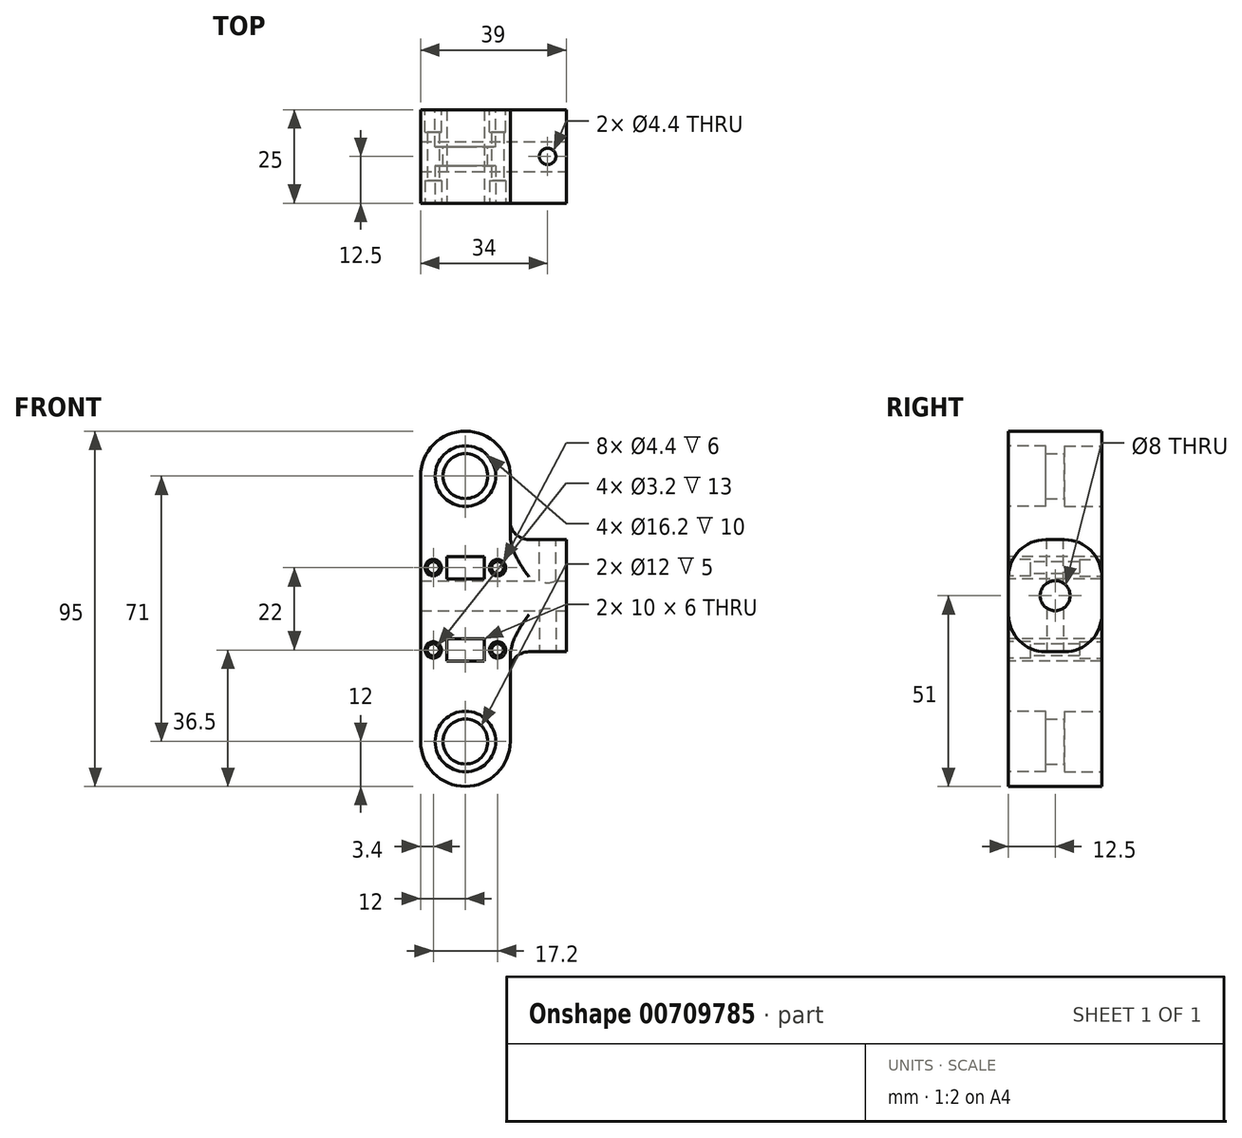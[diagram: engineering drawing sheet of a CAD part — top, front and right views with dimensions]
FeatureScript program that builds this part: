
annotation { "Feature Type Name" : "Feature", "Feature Type Description" : "" }
export const myFeature = defineFeature(function(context is Context, id is Id, definition is map)
    precondition{}
    {
        {
            var Q0;
            Q0=qCreatedBy(makeId("Front.planeOp"),FACE);
            var sketch = newSketch(context, id + "F0", { "sketchPlane" : qUnion([Q0])});
            skCircle(sketch, "E0", {"center": v(0, 35.5) * mm, "radius": 6 * mm});
            skCircle(sketch, "E1", {"center": v(0, -35.5) * mm, "radius": 6 * mm});
            skCircle(sketch, "E2", {"center": v(0, 35.5) * mm, "radius": 12.5 * mm, "construction": true});
            skCircle(sketch, "E3", {"center": v(0, -35.5) * mm, "radius": 12.5 * mm, "construction": true});
            skCircle(sketch, "E4", {"center": v(0, 35.5) * mm, "radius": 8 * mm, "construction": true});
            skCircle(sketch, "E5", {"center": v(0, 35.5) * mm, "radius": 12 * mm});
            skCircle(sketch, "E6", {"center": v(0, -35.5) * mm, "radius": 12 * mm});
            skLineSegment(sketch, "E7", {"start": v(-12, 35.5) * mm, "end": v(-12, -35.5) * mm});
            skLineSegment(sketch, "E8", {"start": v(12, 35.5) * mm, "end": v(12, -35.5) * mm});
            skLineSegment(sketch, "E9", {"start": v(12, 18.5) * mm, "end": v(27, 18.5) * mm});
            skLineSegment(sketch, "E10", {"start": v(27, 18.5) * mm, "end": v(27, -11.5) * mm});
            skLineSegment(sketch, "E11", {"start": v(27, -11.5) * mm, "end": v(12, -11.5) * mm});
            skSolve(sketch);
        }
        {
            var Q0;
            {var subQ4=sQuery(id+"F0.wireOp",EDGE,"E7");Q0=makeQuery(id+"F0.imprint","IMPRINT",FACE,{"disambiguationData":[TD([[makeQuery(id+"F0.imprint","IMPRINT",EDGE,{"derivedFrom":subQ4}),1.0]])]});}
            var Q1;
            Q1=makeQuery(id+"F0.imprint","IMPRINT",FACE,{"disambiguationData":[TD([[makeQuery(id+"F0.imprint","IMPRINT",EDGE,{"derivedFrom":sQuery(id+"F0.wireOp",EDGE,"E0")}),-1.0]])]});
            var Q2;
            Q2=makeQuery(id+"F0.imprint","IMPRINT",FACE,{"disambiguationData":[TD([[makeQuery(id+"F0.imprint","IMPRINT",EDGE,{"derivedFrom":sQuery(id+"F0.wireOp",EDGE,"E1")}),-1.0]])]});
            var Q3;
            {var subQ0=sQuery(id+"F0.wireOp",EDGE,"E9");Q3=makeQuery(id+"F0.imprint","IMPRINT",FACE,{"disambiguationData":[TD([[makeQuery(id+"F0.imprint","IMPRINT",EDGE,{"derivedFrom":subQ0}),-1.0]])]});}
            extrude(context, id + "F1", {"entities" : qUnion([Q0, Q1, Q2, Q3]), "depth" : 25 * mm, "offsetDistance" : 25 * mm});
        }
        {
            var Q0;
            Q0=makeQuery(id+"F1.opExtrude","CAP_FACE",FACE,{"disambiguationData":[OSD([sQuery(id+"F0.wireOp",EDGE,"E0"),sQuery(id+"F0.wireOp",EDGE,"E1"),sQuery(id+"F0.wireOp",EDGE,"E5"),sQuery(id+"F0.wireOp",EDGE,"E6"),sQuery(id+"F0.wireOp",EDGE,"E7"),sQuery(id+"F0.wireOp",EDGE,"E8"),sQuery(id+"F0.wireOp",EDGE,"E9"),sQuery(id+"F0.wireOp",EDGE,"E10"),sQuery(id+"F0.wireOp",EDGE,"E11")])],"isStart":false});
            var sketch = newSketch(context, id + "F2", { "sketchPlane" : qUnion([Q0])});
            skCircle(sketch, "E12", {"center": v(0, 35.5) * mm, "radius": 8.1 * mm});
            skCircle(sketch, "E13", {"center": v(0, -35.5) * mm, "radius": 8.1 * mm});
            skSolve(sketch);
        }
        {
            var Q0;
            Q0=makeQuery(id+"F2.imprint","IMPRINT",FACE,{"disambiguationData":[TD([[makeQuery(id+"F2.imprint","IMPRINT",EDGE,{"derivedFrom":sQuery(id+"F2.wireOp",EDGE,"E12")}),1.0]])]});
            var Q1;
            Q1=makeQuery(id+"F2.imprint","IMPRINT",FACE,{"disambiguationData":[TD([[makeQuery(id+"F2.imprint","IMPRINT",EDGE,{"derivedFrom":sQuery(id+"F2.wireOp",EDGE,"E13")}),1.0]])]});
            extrude(context, id + "F3", {"entities" : qUnion([Q0, Q1]), "operationType" : NewBodyOperationType.REMOVE, "oppositeDirection" : true, "depth" : 10 * mm, "offsetDistance" : 25 * mm});
        }
        {
            var Q0;
            Q0=makeQuery(id+"F1.opExtrude","CAP_FACE",FACE,{"disambiguationData":[OSD([sQuery(id+"F0.wireOp",EDGE,"E0"),sQuery(id+"F0.wireOp",EDGE,"E1"),sQuery(id+"F0.wireOp",EDGE,"E5"),sQuery(id+"F0.wireOp",EDGE,"E6"),sQuery(id+"F0.wireOp",EDGE,"E7"),sQuery(id+"F0.wireOp",EDGE,"E8"),sQuery(id+"F0.wireOp",EDGE,"E9"),sQuery(id+"F0.wireOp",EDGE,"E10"),sQuery(id+"F0.wireOp",EDGE,"E11")])],"isStart":true});
            var sketch = newSketch(context, id + "F4", { "sketchPlane" : qUnion([Q0])});
            skCircle(sketch, "E14.0", {"center": v(0, 35.5) * mm, "radius": 8.1 * mm});
            skCircle(sketch, "E15.0", {"center": v(0, -35.5) * mm, "radius": 8.1 * mm});
            skSolve(sketch);
        }
        {
            var Q0;
            Q0=makeQuery(id+"F4.imprint","IMPRINT",FACE,{"disambiguationData":[TD([[makeQuery(id+"F4.imprint","IMPRINT",EDGE,{"derivedFrom":sQuery(id+"F4.wireOp",EDGE,"E14.0")}),1.0]])]});
            var Q1;
            Q1=makeQuery(id+"F4.imprint","IMPRINT",FACE,{"disambiguationData":[TD([[makeQuery(id+"F4.imprint","IMPRINT",EDGE,{"derivedFrom":sQuery(id+"F4.wireOp",EDGE,"E15.0")}),1.0]])]});
            extrude(context, id + "F5", {"entities" : qUnion([Q0, Q1]), "operationType" : NewBodyOperationType.REMOVE, "oppositeDirection" : true, "depth" : 10 * mm, "offsetDistance" : 25 * mm});
        }
        {
            var Q0;
            Q0=makeQuery(id+"F1.opExtrude","SWEPT_FACE",FACE,{"disambiguationData":[OSD([sQuery(id+"F0.wireOp",EDGE,"E10")])]});
            var sketch = newSketch(context, id + "F6", { "sketchPlane" : qUnion([Q0])});
            skCircle(sketch, "E16", {"center": v(-12.5, 3.5) * mm, "radius": 4 * mm});
            skPoint(sketch, "E16.centerSnap0", {"position": v(-12.5, 18.5) * mm});
            skSolve(sketch);
        }
        {
            var Q0;
            Q0=makeQuery(id+"F6.imprint","IMPRINT",FACE,{"disambiguationData":[TD([[makeQuery(id+"F6.imprint","IMPRINT",EDGE,{"derivedFrom":sQuery(id+"F6.wireOp",EDGE,"E16")}),1.0]])]});
            extrude(context, id + "F7", {"entities" : qUnion([Q0]), "operationType" : NewBodyOperationType.REMOVE, "endBound" : BoundingType.THROUGH_ALL, "oppositeDirection" : true, "depth" : 25 * mm, "offsetDistance" : 25 * mm});
        }
        {
            var Q0;
            Q0=makeQuery(id+"F1.opExtrude","CAP_EDGE",EDGE,{"disambiguationData":[OSD([sQuery(id+"F0.wireOp",EDGE,"E9")])],"isStart":false});
            var Q1;
            Q1=makeQuery(id+"F1.opExtrude","CAP_EDGE",EDGE,{"disambiguationData":[OSD([sQuery(id+"F0.wireOp",EDGE,"E9")])],"isStart":true});
            var Q2;
            Q2=makeQuery(id+"F1.opExtrude","CAP_EDGE",EDGE,{"disambiguationData":[OSD([sQuery(id+"F0.wireOp",EDGE,"E11")])],"isStart":false});
            var Q3;
            Q3=makeQuery(id+"F1.opExtrude","CAP_EDGE",EDGE,{"disambiguationData":[OSD([sQuery(id+"F0.wireOp",EDGE,"E11")])],"isStart":true});
            fillet(context, id + "F8", {"entities" : qUnion([Q0, Q1, Q2, Q3]), "radius" : 10 * mm, "allowEdgeOverflow" : false});
        }
        {
            var Q0;
            Q0=makeQuery(id+"F1.opExtrude","SWEPT_EDGE",EDGE,{"disambiguationData":[OSD([sQuery(id+"F0.wireOp",EDGE,"E8"),sQuery(id+"F0.wireOp",EDGE,"E9")])]});
            var Q1;
            Q1=makeQuery(id+"F1.opExtrude","SWEPT_EDGE",EDGE,{"disambiguationData":[OSD([sQuery(id+"F0.wireOp",EDGE,"E8"),sQuery(id+"F0.wireOp",EDGE,"E11")])]});
            fillet(context, id + "F9", {"entities" : qUnion([Q0, Q1]), "radius" : 5 * mm, "tangentPropagation" : true, "allowEdgeOverflow" : false});
        }
        {
            var Q0;
            Q0=makeQuery(id+"F1.opExtrude","SWEPT_FACE",FACE,{"disambiguationData":[OSD([sQuery(id+"F0.wireOp",EDGE,"E9")])]});
            var sketch = newSketch(context, id + "F10", { "sketchPlane" : qUnion([Q0])});
            skCircle(sketch, "E17", {"center": v(22, -12.5) * mm, "radius": 2.2 * mm});
            skPoint(sketch, "E17.centerSnap0", {"position": v(17, -12.5) * mm});
            skPoint(sketch, "E17.centerSnap1", {"position": v(22, -10) * mm});
            skSolve(sketch);
        }
        {
            var Q0;
            Q0=makeQuery(id+"F10.imprint","IMPRINT",FACE,{"disambiguationData":[TD([[makeQuery(id+"F10.imprint","IMPRINT",EDGE,{"derivedFrom":sQuery(id+"F10.wireOp",EDGE,"E17")}),1.0]])]});
            extrude(context, id + "F11", {"entities" : qUnion([Q0]), "operationType" : NewBodyOperationType.REMOVE, "endBound" : BoundingType.UP_TO_NEXT, "oppositeDirection" : true, "depth" : 25 * mm, "offsetDistance" : 25 * mm});
        }
        {
            var Q0;
            Q0=makeQuery(id+"F1.opExtrude","SWEPT_FACE",FACE,{"disambiguationData":[OSD([sQuery(id+"F0.wireOp",EDGE,"E11")])]});
            var sketch = newSketch(context, id + "F12", { "sketchPlane" : qUnion([Q0])});
            skCircle(sketch, "E18.0", {"center": v(22, 12.5) * mm, "radius": 2.2 * mm});
            skSolve(sketch);
        }
        {
            var Q0;
            Q0=makeQuery(id+"F12.imprint","IMPRINT",FACE,{"disambiguationData":[TD([[makeQuery(id+"F12.imprint","IMPRINT",EDGE,{"derivedFrom":sQuery(id+"F12.wireOp",EDGE,"E18.0")}),1.0]])]});
            extrude(context, id + "F13", {"entities" : qUnion([Q0]), "operationType" : NewBodyOperationType.REMOVE, "endBound" : BoundingType.UP_TO_NEXT, "oppositeDirection" : true, "depth" : 25 * mm, "offsetDistance" : 25 * mm});
        }
        {
            var Q0;
            Q0=makeQuery(id+"F1.opExtrude","CAP_FACE",FACE,{"disambiguationData":[OSD([sQuery(id+"F0.wireOp",EDGE,"E0"),sQuery(id+"F0.wireOp",EDGE,"E1"),sQuery(id+"F0.wireOp",EDGE,"E5"),sQuery(id+"F0.wireOp",EDGE,"E6"),sQuery(id+"F0.wireOp",EDGE,"E7"),sQuery(id+"F0.wireOp",EDGE,"E8"),sQuery(id+"F0.wireOp",EDGE,"E9"),sQuery(id+"F0.wireOp",EDGE,"E10"),sQuery(id+"F0.wireOp",EDGE,"E11")])],"isStart":false});
            var sketch = newSketch(context, id + "F14", { "sketchPlane" : qUnion([Q0])});
            skLineSegment(sketch, "E19.bottom", {"start": v(-3, 12) * mm, "end": v(3, 12) * mm, "construction": true});
            skLineSegment(sketch, "E19.top", {"start": v(-3, 10) * mm, "end": v(3, 10) * mm, "construction": true});
            skLineSegment(sketch, "E19.left", {"start": v(-3, 12) * mm, "end": v(-3, 10) * mm, "construction": true});
            skLineSegment(sketch, "E19.right", {"start": v(3, 12) * mm, "end": v(3, 10) * mm, "construction": true});
            skLineSegment(sketch, "E20.bottom", {"start": v(-3, -10) * mm, "end": v(3, -10) * mm, "construction": true});
            skLineSegment(sketch, "E20.top", {"start": v(-3, -12) * mm, "end": v(3, -12) * mm, "construction": true});
            skLineSegment(sketch, "E20.left", {"start": v(-3, -10) * mm, "end": v(-3, -12) * mm, "construction": true});
            skLineSegment(sketch, "E20.right", {"start": v(3, -10) * mm, "end": v(3, -12) * mm, "construction": true});
            skLineSegment(sketch, "E21", {"start": v(0, 0) * mm, "end": v(0, -10) * mm, "construction": true});
            skLineSegment(sketch, "E22.bottom", {"start": v(5, 8) * mm, "end": v(-5, 8) * mm});
            skLineSegment(sketch, "E22.top", {"start": v(5, 14) * mm, "end": v(-5, 14) * mm});
            skLineSegment(sketch, "E22.left", {"start": v(5, 8) * mm, "end": v(5, 14) * mm});
            skLineSegment(sketch, "E22.right", {"start": v(-5, 8) * mm, "end": v(-5, 14) * mm});
            skPoint(sketch, "E22.middle", {"position": v(0, 11) * mm});
            skPoint(sketch, "E22.middle.positionSnap0", {"position": v(0, 12) * mm});
            skPoint(sketch, "E22.middle.positionSnap1", {"position": v(3, 11) * mm});
            skPoint(sketch, "E22.centerSnap0", {"position": v(0, 12) * mm});
            skPoint(sketch, "E22.centerSnap1", {"position": v(3, 11) * mm});
            skLineSegment(sketch, "E23.bottom", {"start": v(5, -14) * mm, "end": v(-5, -14) * mm});
            skLineSegment(sketch, "E23.top", {"start": v(5, -8) * mm, "end": v(-5, -8) * mm});
            skLineSegment(sketch, "E23.left", {"start": v(5, -14) * mm, "end": v(5, -8) * mm});
            skLineSegment(sketch, "E23.right", {"start": v(-5, -14) * mm, "end": v(-5, -8) * mm});
            skPoint(sketch, "E23.middle", {"position": v(0, -11) * mm});
            skPoint(sketch, "E23.middle.positionSnap0", {"position": v(3, -11) * mm});
            skPoint(sketch, "E23.middle.positionSnap1", {"position": v(0, -12) * mm});
            skPoint(sketch, "E23.centerSnap0", {"position": v(3, -11) * mm});
            skPoint(sketch, "E23.centerSnap1", {"position": v(0, -12) * mm});
            skCircle(sketch, "E24", {"center": v(-8.6, 11) * mm, "radius": 1.6 * mm});
            skPoint(sketch, "E24.centerSnap0", {"position": v(-5, 11) * mm});
            skCircle(sketch, "E25", {"center": v(8.6, 11) * mm, "radius": 1.6 * mm});
            skPoint(sketch, "E25.centerSnap0", {"position": v(5, 11) * mm});
            skCircle(sketch, "E26", {"center": v(-8.6, -11) * mm, "radius": 1.6 * mm});
            skPoint(sketch, "E26.centerSnap0", {"position": v(-5, -11) * mm});
            skCircle(sketch, "E27", {"center": v(8.6, -11) * mm, "radius": 1.6 * mm});
            skPoint(sketch, "E27.centerSnap0", {"position": v(5, -11) * mm});
            skSolve(sketch);
        }
        {
            var Q0;
            Q0=makeQuery(id+"F14.imprint","IMPRINT",FACE,{"disambiguationData":[TD([[makeQuery(id+"F14.imprint","IMPRINT",EDGE,{"derivedFrom":sQuery(id+"F14.wireOp",EDGE,"E24")}),1.0]])]});
            var Q1;
            Q1=makeQuery(id+"F14.imprint","IMPRINT",FACE,{"disambiguationData":[TD([[makeQuery(id+"F14.imprint","IMPRINT",EDGE,{"derivedFrom":sQuery(id+"F14.wireOp",EDGE,"E22.bottom")}),-1.0]])]});
            var Q2;
            Q2=makeQuery(id+"F14.imprint","IMPRINT",FACE,{"disambiguationData":[TD([[makeQuery(id+"F14.imprint","IMPRINT",EDGE,{"derivedFrom":sQuery(id+"F14.wireOp",EDGE,"E25")}),1.0]])]});
            var Q3;
            Q3=makeQuery(id+"F14.imprint","IMPRINT",FACE,{"disambiguationData":[TD([[makeQuery(id+"F14.imprint","IMPRINT",EDGE,{"derivedFrom":sQuery(id+"F14.wireOp",EDGE,"E27")}),1.0]])]});
            var Q4;
            Q4=makeQuery(id+"F14.imprint","IMPRINT",FACE,{"disambiguationData":[TD([[makeQuery(id+"F14.imprint","IMPRINT",EDGE,{"derivedFrom":sQuery(id+"F14.wireOp",EDGE,"E23.bottom")}),-1.0]])]});
            var Q5;
            Q5=makeQuery(id+"F14.imprint","IMPRINT",FACE,{"disambiguationData":[TD([[makeQuery(id+"F14.imprint","IMPRINT",EDGE,{"derivedFrom":sQuery(id+"F14.wireOp",EDGE,"E26")}),1.0]])]});
            extrude(context, id + "F15", {"entities" : qUnion([Q0, Q1, Q2, Q3, Q4, Q5]), "operationType" : NewBodyOperationType.REMOVE, "endBound" : BoundingType.THROUGH_ALL, "oppositeDirection" : true, "depth" : 25 * mm, "offsetDistance" : 25 * mm});
        }
        {
            var Q0;
            Q0=makeQuery(id+"F1.opExtrude","CAP_FACE",FACE,{"disambiguationData":[OSD([sQuery(id+"F0.wireOp",EDGE,"E0"),sQuery(id+"F0.wireOp",EDGE,"E1"),sQuery(id+"F0.wireOp",EDGE,"E5"),sQuery(id+"F0.wireOp",EDGE,"E6"),sQuery(id+"F0.wireOp",EDGE,"E7"),sQuery(id+"F0.wireOp",EDGE,"E8"),sQuery(id+"F0.wireOp",EDGE,"E9"),sQuery(id+"F0.wireOp",EDGE,"E10"),sQuery(id+"F0.wireOp",EDGE,"E11")])],"isStart":false});
            var sketch = newSketch(context, id + "F16", { "sketchPlane" : qUnion([Q0])});
            skCircle(sketch, "E28", {"center": v(-8.6, 11) * mm, "radius": 2.2 * mm});
            skCircle(sketch, "E29", {"center": v(8.6, 11) * mm, "radius": 2.2 * mm});
            skCircle(sketch, "E30", {"center": v(8.6, -11) * mm, "radius": 2.2 * mm});
            skCircle(sketch, "E31", {"center": v(-8.6, -11) * mm, "radius": 2.2 * mm});
            skSolve(sketch);
        }
        {
            var Q0;
            Q0=makeQuery(id+"F16.imprint","IMPRINT",FACE,{"disambiguationData":[TD([[makeQuery(id+"F16.imprint","IMPRINT",EDGE,{"derivedFrom":sQuery(id+"F16.wireOp",EDGE,"E28")}),1.0]])]});
            var Q1;
            Q1=makeQuery(id+"F16.imprint","IMPRINT",FACE,{"disambiguationData":[TD([[makeQuery(id+"F16.imprint","IMPRINT",EDGE,{"derivedFrom":sQuery(id+"F16.wireOp",EDGE,"E29")}),1.0]])]});
            var Q2;
            Q2=makeQuery(id+"F16.imprint","IMPRINT",FACE,{"disambiguationData":[TD([[makeQuery(id+"F16.imprint","IMPRINT",EDGE,{"derivedFrom":sQuery(id+"F16.wireOp",EDGE,"E30")}),1.0]])]});
            var Q3;
            Q3=makeQuery(id+"F16.imprint","IMPRINT",FACE,{"disambiguationData":[TD([[makeQuery(id+"F16.imprint","IMPRINT",EDGE,{"derivedFrom":sQuery(id+"F16.wireOp",EDGE,"E31")}),1.0]])]});
            extrude(context, id + "F17", {"entities" : qUnion([Q0, Q1, Q2, Q3]), "operationType" : NewBodyOperationType.REMOVE, "oppositeDirection" : true, "depth" : 6 * mm, "offsetDistance" : 25 * mm});
        }
        {
            var Q0;
            Q0=makeQuery(id+"F1.opExtrude","CAP_FACE",FACE,{"disambiguationData":[OSD([sQuery(id+"F0.wireOp",EDGE,"E0"),sQuery(id+"F0.wireOp",EDGE,"E1"),sQuery(id+"F0.wireOp",EDGE,"E5"),sQuery(id+"F0.wireOp",EDGE,"E6"),sQuery(id+"F0.wireOp",EDGE,"E7"),sQuery(id+"F0.wireOp",EDGE,"E8"),sQuery(id+"F0.wireOp",EDGE,"E9"),sQuery(id+"F0.wireOp",EDGE,"E10"),sQuery(id+"F0.wireOp",EDGE,"E11")])],"isStart":true});
            var sketch = newSketch(context, id + "F18", { "sketchPlane" : qUnion([Q0])});
            skCircle(sketch, "E32.0", {"center": v(8.6, 11) * mm, "radius": 2.2 * mm});
            skCircle(sketch, "E33.0", {"center": v(-8.6, 11) * mm, "radius": 2.2 * mm});
            skCircle(sketch, "E34.0", {"center": v(-8.6, -11) * mm, "radius": 2.2 * mm});
            skCircle(sketch, "E35.0", {"center": v(8.6, -11) * mm, "radius": 2.2 * mm});
            skSolve(sketch);
        }
        {
            var Q0;
            Q0 = qSketchRegion(id + "F18", true);
            extrude(context, id + "F19", {"entities" : qUnion([Q0]), "operationType" : NewBodyOperationType.REMOVE, "oppositeDirection" : true, "depth" : 6 * mm, "offsetDistance" : 25 * mm});
        }
    });
